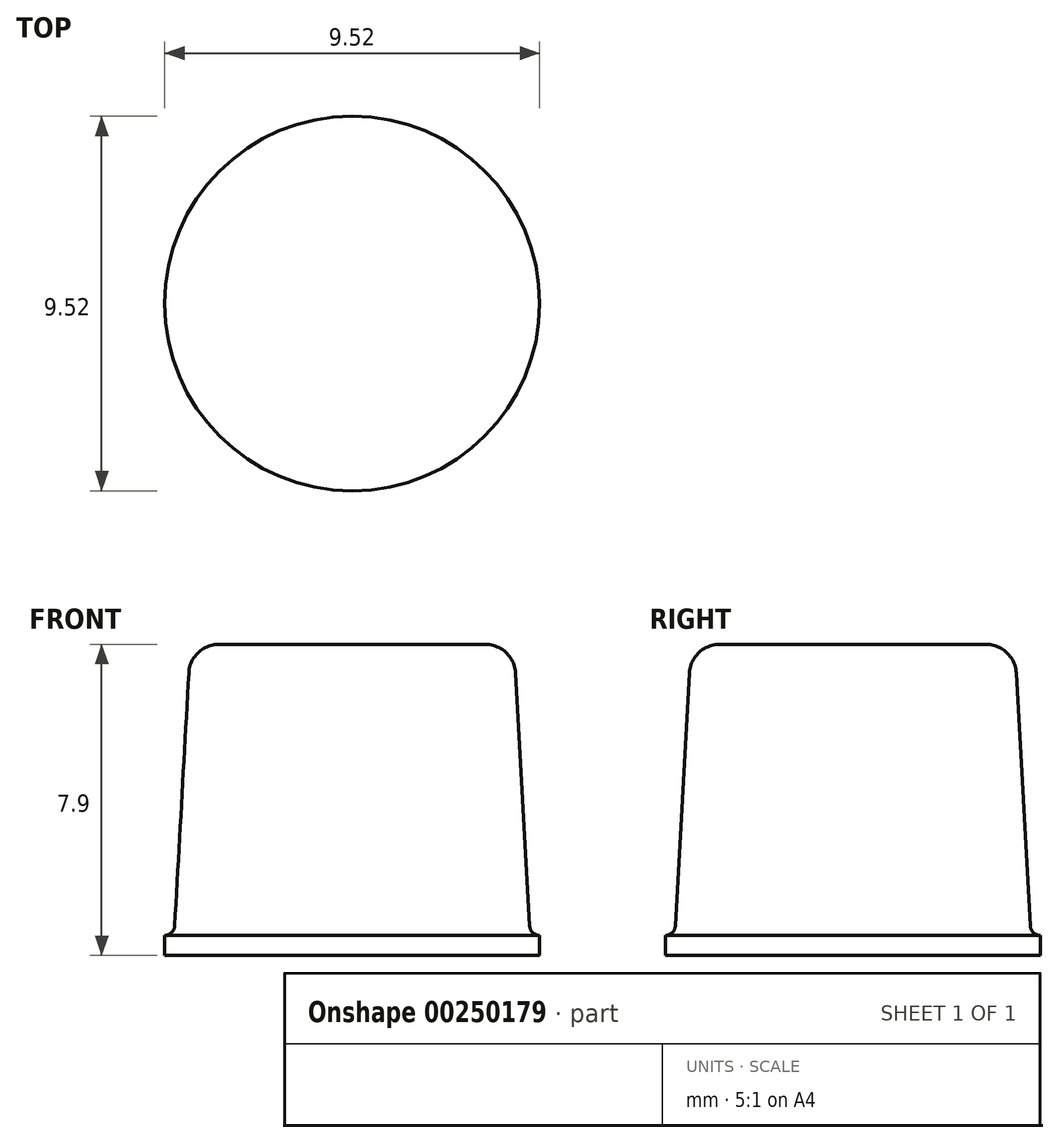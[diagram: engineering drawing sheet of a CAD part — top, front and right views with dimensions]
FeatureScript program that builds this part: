
annotation { "Feature Type Name" : "Feature", "Feature Type Description" : "" }
export const myFeature = defineFeature(function(context is Context, id is Id, definition is map)
    precondition{}
    {
        {
            var Q0;
            Q0=qCreatedBy(makeId("Front.planeOp"),FACE);
            var sketch = newSketch(context, id + "F0", { "sketchPlane" : qUnion([Q0])});
            skLineSegment(sketch, "E0", {"start": v(-4.76, 0) * mm, "end": v(0, 0) * mm});
            skLineSegment(sketch, "E1.0", {"start": v(-4.76, 0.5) * mm, "end": v(0, 0.5) * mm});
            skLineSegment(sketch, "E2.0", {"start": v(-3.39, 7.9) * mm, "end": v(0, 7.9) * mm});
            skLineSegment(sketch, "E3", {"start": v(-4.15, 7.18) * mm, "end": v(-4.5, 0.75) * mm});
            skLineSegment(sketch, "E4", {"start": v(-4.76, 0.5) * mm, "end": v(-4.76, 0) * mm});
            skArc(sketch, "E5", {"start": v(-4.5, 0.75) * mm, "mid": v(-4.59, 0.58) * mm, "end": v(-4.76, 0.5) * mm});
            skPoint(sketch, "E6.visualSharp", {"position": v(-4.1, 7.9) * mm});
            skArc(sketch, "E6.filletArc", {"start": v(-3.39, 7.9) * mm, "mid": v(-3.91, 7.7) * mm, "end": v(-4.15, 7.18) * mm});
            skLineSegment(sketch, "E7", {"start": v(0, 0) * mm, "end": v(0, 7.9) * mm});
            skPoint(sketch, "E7.endSnap0", {"position": v(0, 0.5) * mm});
            skPoint(sketch, "E8.orphan", {"position": v(4.76, 0.5) * mm});
            skLineSegment(sketch, "E9.MirrorCS", {"start": v(3.39, 7.9) * mm, "end": v(0, 7.9) * mm});
            skArc(sketch, "E10.MirrorCS", {"start": v(3.39, 7.9) * mm, "mid": v(3.91, 7.7) * mm, "end": v(4.15, 7.18) * mm});
            skLineSegment(sketch, "E11.MirrorCS", {"start": v(4.15, 7.18) * mm, "end": v(4.5, 0.75) * mm});
            skArc(sketch, "E12.MirrorCS", {"start": v(4.5, 0.75) * mm, "mid": v(4.59, 0.58) * mm, "end": v(4.76, 0.5) * mm});
            skLineSegment(sketch, "E13.MirrorCS", {"start": v(4.76, 0.5) * mm, "end": v(4.76, 0) * mm});
            skLineSegment(sketch, "E14.MirrorCS", {"start": v(4.76, 0) * mm, "end": v(0, 0) * mm});
            skSolve(sketch);
        }
        {
            var Q0;
            {var subQ0=sQuery(id+"F0.wireOp",EDGE,"E9.MirrorCS");Q0=makeQuery(id+"F0.imprint","IMPRINT",FACE,{"disambiguationData":[TD([[makeQuery(id+"F0.imprint","IMPRINT",EDGE,{"derivedFrom":subQ0}),1.0]])]});}
            var Q1;
            Q1=sQuery(id+"F0.wireOp",EDGE,"E7");
            revolve(context, id + "F1", {"entities" : qUnion([Q0]), "axis" : qUnion([Q1]), "revolveType" : RevolveType.FULL});
        }
    });
